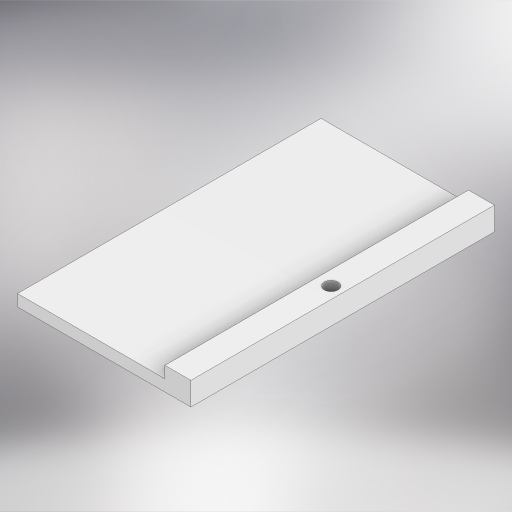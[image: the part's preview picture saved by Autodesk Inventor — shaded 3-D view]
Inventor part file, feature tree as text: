
AUTODESK INVENTOR PART (.ipt)
format: ipt  version: 2024 (Build 280153000, 153)  size: 291,840 bytes
history: native  units: in
note: dims shown in document units (in); Inventor stores cm internally (conversion verified against a paired STEP export)
features: sketch x3, extrude x2, hole x1
ambient origin geometry x8: Origin, YZ Plane, XZ Plane, XY Plane, X Axis, Y Axis, Z Axis, Center Point
bodies: Solid1 (feature_tree)
feature tree (6):
  extrude  "Extrusion1"  Depth=1.1811in
  extrude  "Extrusion2"  Depth=0.0787in TaperAngle=0.0deg
  hole  "Hole2"  [1 undecoded]
  sketch  "Sketch1"  dims[d0=2.0669in d1=1.1811in]
  sketch  "Sketch2"  dims[d2=0.1575in d3=0.0in d5=0.0787in d6=0.0in]
  sketch  "Sketch4"  dims[d19=0.0945in d20=0.2362in d21=0.1181in d22=0.0787in d23=90.0deg d24=0.315in d25=0.8108in d26=0.1772in d28=0.0787in]
note: 1 required parameter value undecoded (feature->parameter linkage not recoverable at this tier; creation-order binding heuristic only, values carry confidence <= 0.55)
